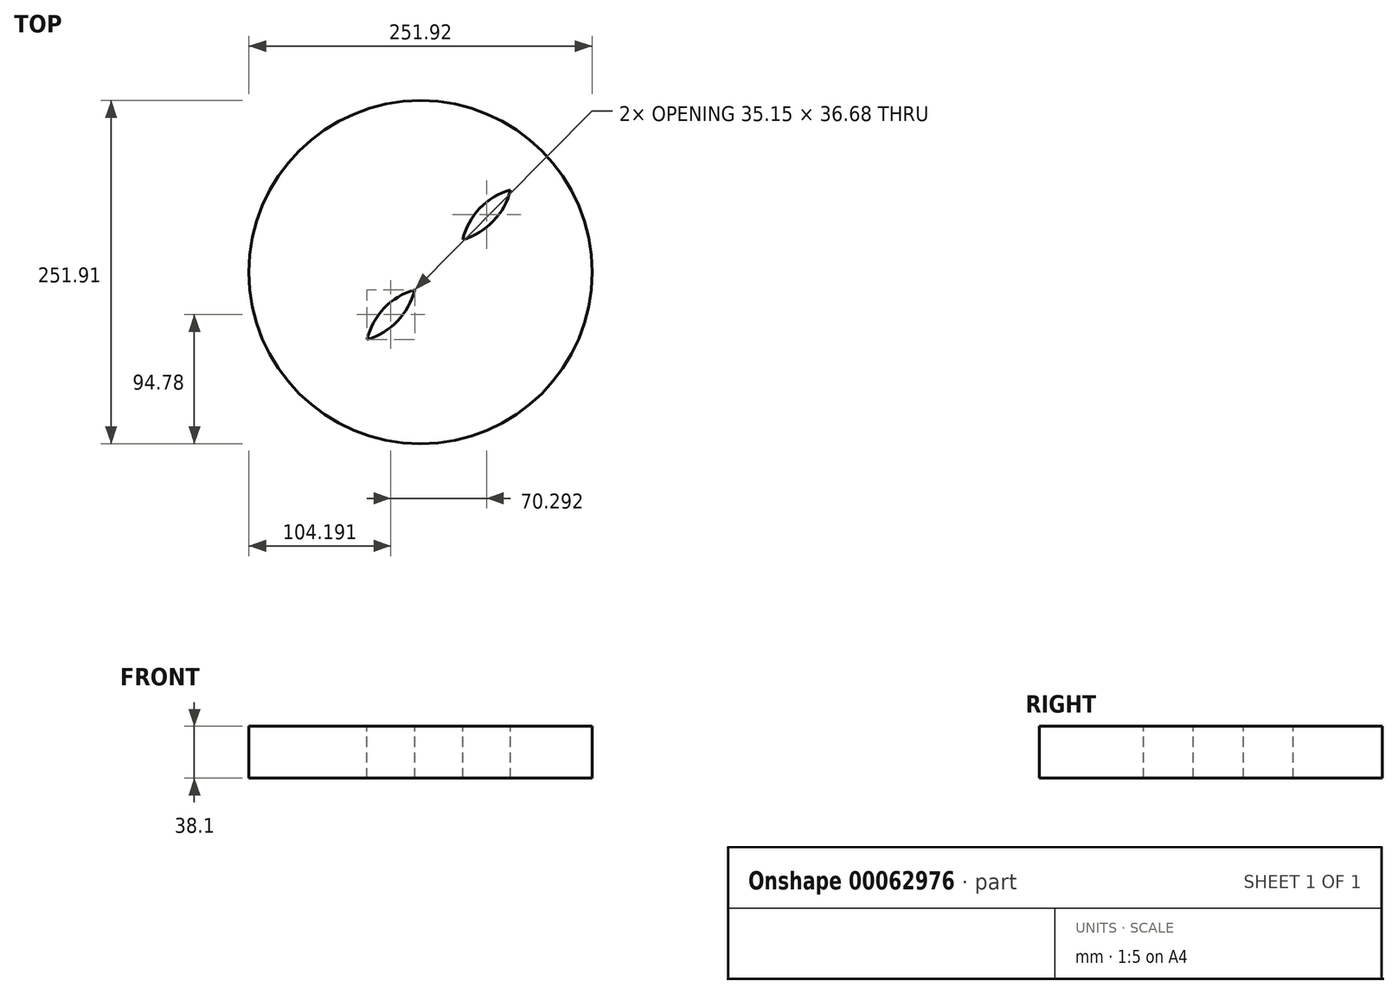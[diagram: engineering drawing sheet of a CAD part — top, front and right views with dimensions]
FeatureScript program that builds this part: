
annotation { "Feature Type Name" : "Feature", "Feature Type Description" : "" }
export const myFeature = defineFeature(function(context is Context, id is Id, definition is map)
    precondition{}
    {
        {
            var Q0;
            Q0=qCreatedBy(makeId("Top.planeOp"),FACE);
            var sketch = newSketch(context, id + "F0", { "sketchPlane" : qUnion([Q0])});
            skCircle(sketch, "E0", {"center": v(-30.95, -23.85) * mm, "radius": 125.96 * mm});
            skSolve(sketch);
        }
        {
            var Q0;
            Q0=makeQuery(id+"F0.imprint","IMPRINT",FACE,{"disambiguationData":[TD([[makeQuery(id+"F0.imprint","IMPRINT",EDGE,{"derivedFrom":sQuery(id+"F0.wireOp",EDGE,"E0")}),1.0]])]});
            extrude(context, id + "F1", {"entities" : qUnion([Q0]), "oppositeDirection" : true, "depth" : 38.1 * mm});
        }
        {
            var Q0;
            Q0=qCreatedBy(makeId("Top.planeOp"),FACE);
            var sketch = newSketch(context, id + "F2", { "sketchPlane" : qUnion([Q0])});
            skCircle(sketch, "E1", {"center": v(0, 0) * mm, "radius": 50.8 * mm});
            skCircle(sketch, "E2", {"center": v(35.15, 36.68) * mm, "radius": 50.8 * mm});
            skCircle(sketch, "E3", {"center": v(-14.2, 48.78) * mm, "radius": 50.8 * mm});
            skCircle(sketch, "E4", {"center": v(-49.34, 12.1) * mm, "radius": 50.8 * mm});
            skCircle(sketch, "E5", {"center": v(-35.15, -36.68) * mm, "radius": 50.8 * mm});
            skCircle(sketch, "E6", {"center": v(14.2, -48.78) * mm, "radius": 50.8 * mm});
            skCircle(sketch, "E7", {"center": v(49.34, -12.1) * mm, "radius": 50.8 * mm});
            skCircle(sketch, "E8", {"center": v(-84.48, -24.58) * mm, "radius": 50.8 * mm});
            skCircle(sketch, "E9", {"center": v(-20.95, -85.46) * mm, "radius": 50.8 * mm});
            skSolve(sketch);
        }
        {
            var Q0;
            {var subQ0=sQuery(id+"F2.wireOp",EDGE,"E9");var subQ1=sQuery(id+"F2.wireOp",EDGE,"E8");var subQ2=makeQuery(id+"F2.imprint","INTERSECT",VERTEX,{"derivedFrom":[sQuery(id+"F2.wireOp",EDGE,"E5"),subQ1,subQ0]});Q0=makeQuery(id+"F2.imprint","IMPRINT",FACE,{"disambiguationData":[TD([[makeQuery(id+"F2.imprint","IMPRINT",EDGE,{"disambiguationData":[TD([[subQ2,-1.0]])],"derivedFrom":subQ1}),1.0]])]});}
            var Q1;
            {var subQ0=sQuery(id+"F2.wireOp",EDGE,"E7");var subQ1=sQuery(id+"F2.wireOp",EDGE,"E3");var subQ2=makeQuery(id+"F2.imprint","INTERSECT",VERTEX,{"derivedFrom":[sQuery(id+"F2.wireOp",EDGE,"E1"),subQ1,subQ0]});Q1=makeQuery(id+"F2.imprint","IMPRINT",FACE,{"disambiguationData":[TD([[makeQuery(id+"F2.imprint","IMPRINT",EDGE,{"disambiguationData":[TD([[subQ2,1.0]])],"derivedFrom":subQ1}),1.0]])]});}
            extrude(context, id + "F3", {"entities" : qUnion([Q0, Q1]), "operationType" : NewBodyOperationType.REMOVE, "endBound" : BoundingType.THROUGH_ALL, "oppositeDirection" : true, "depth" : 25.4 * mm});
        }
    });
